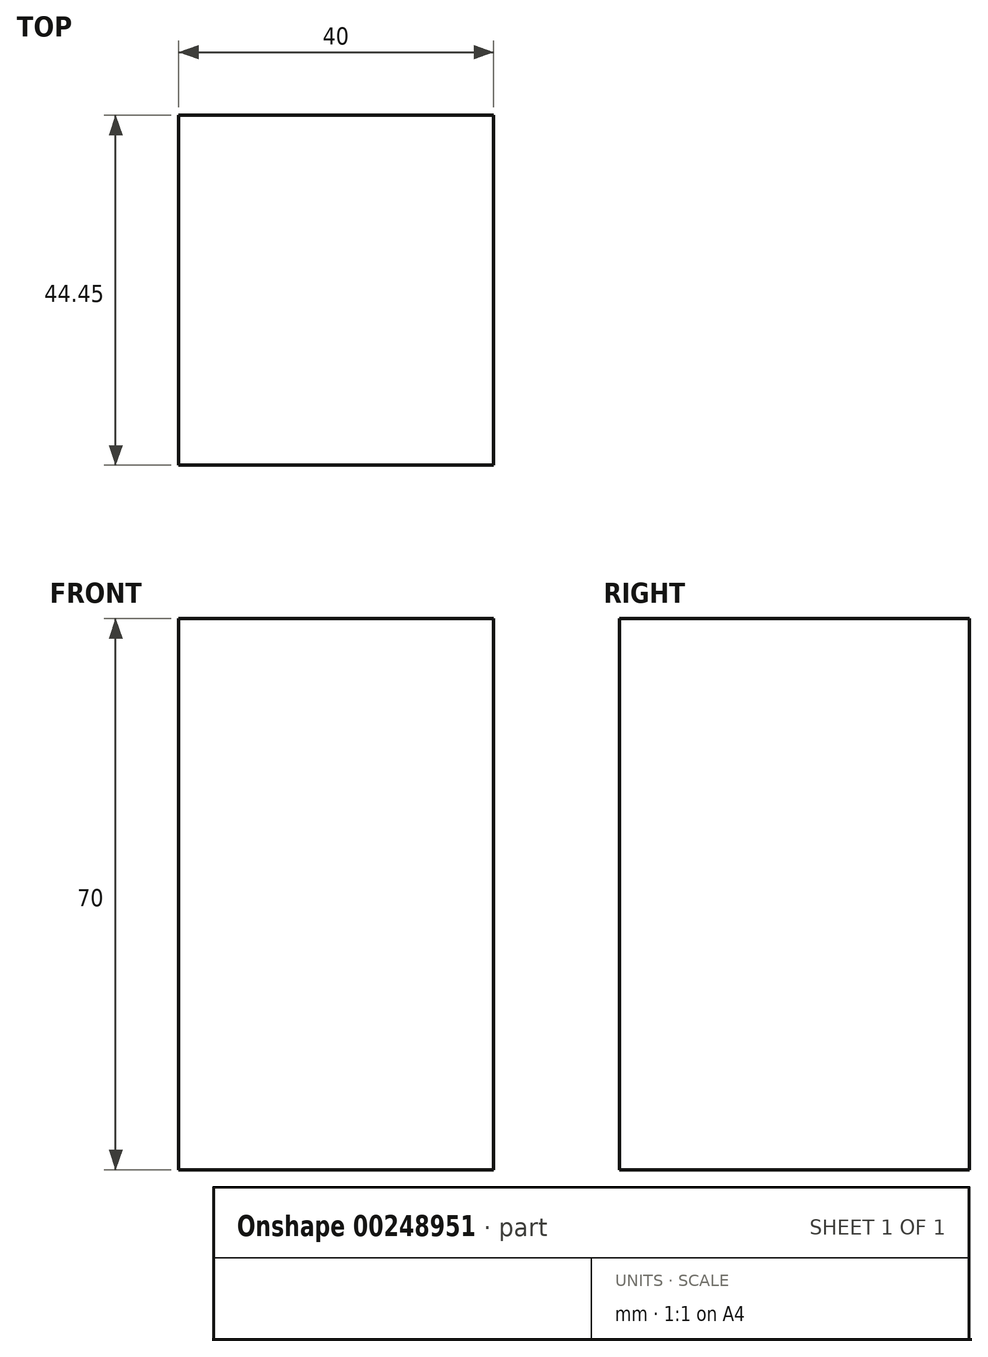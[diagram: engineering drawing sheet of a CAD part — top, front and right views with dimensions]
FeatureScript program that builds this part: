
annotation { "Feature Type Name" : "Feature", "Feature Type Description" : "" }
export const myFeature = defineFeature(function(context is Context, id is Id, definition is map)
    precondition{}
    {
        {
            var Q0;
            Q0=qCreatedBy(makeId("Front.planeOp"),FACE);
            var sketch = newSketch(context, id + "F0", { "sketchPlane" : qUnion([Q0])});
            skLineSegment(sketch, "E0.bottom", {"start": v(-42.99, -49.84) * mm, "end": v(-2.99, -49.84) * mm});
            skLineSegment(sketch, "E0.top", {"start": v(-42.99, -119.84) * mm, "end": v(-2.99, -119.84) * mm});
            skLineSegment(sketch, "E0.left", {"start": v(-42.99, -49.84) * mm, "end": v(-42.99, -119.84) * mm});
            skLineSegment(sketch, "E0.right", {"start": v(-2.99, -49.84) * mm, "end": v(-2.99, -119.84) * mm});
            skSolve(sketch);
        }
        {
            var Q0;
            Q0=makeQuery(id+"F0.imprint","IMPRINT",FACE,{"disambiguationData":[TD([[makeQuery(id+"F0.imprint","IMPRINT",EDGE,{"derivedFrom":sQuery(id+"F0.wireOp",EDGE,"E0.bottom")}),-1.0]])]});
            extrude(context, id + "F1", {"entities" : qUnion([Q0]), "depth" : 44.45 * mm});
        }
    });
